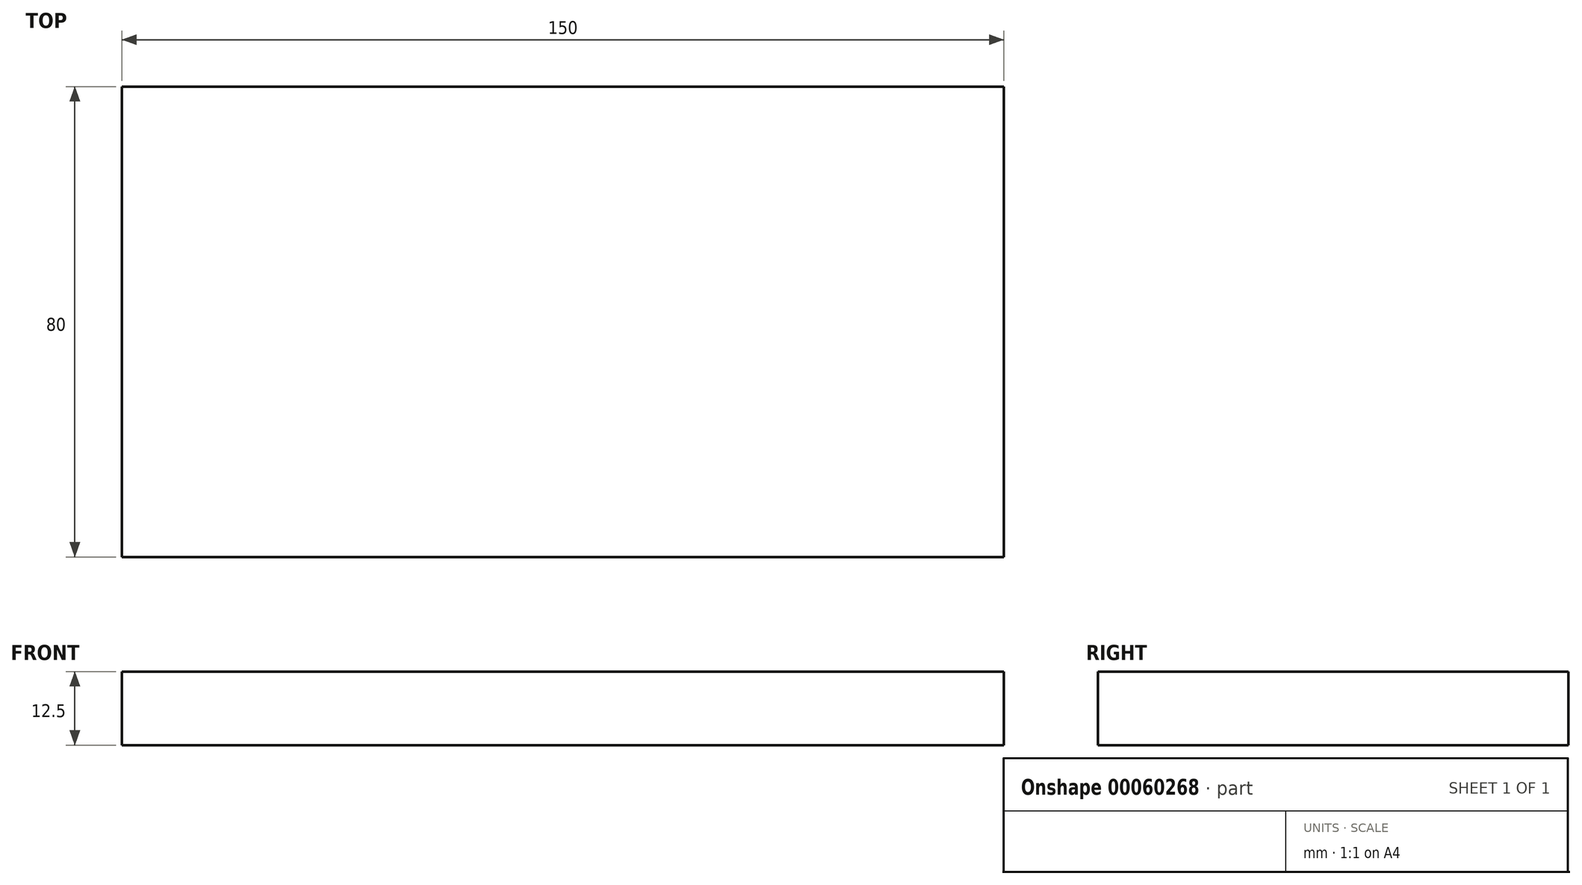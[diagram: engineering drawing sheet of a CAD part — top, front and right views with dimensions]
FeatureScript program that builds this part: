
annotation { "Feature Type Name" : "Feature", "Feature Type Description" : "" }
export const myFeature = defineFeature(function(context is Context, id is Id, definition is map)
    precondition{}
    {
        {
            var Q0;
            Q0=qCreatedBy(makeId("Top.planeOp"),FACE);
            var sketch = newSketch(context, id + "F0", { "sketchPlane" : qUnion([Q0])});
            skLineSegment(sketch, "E0.rect.bottom", {"start": v(-75, 40) * mm, "end": v(75, 40) * mm});
            skLineSegment(sketch, "E0.rect.top", {"start": v(-75, -40) * mm, "end": v(75, -40) * mm});
            skLineSegment(sketch, "E0.rect.left", {"start": v(-75, 40) * mm, "end": v(-75, -40) * mm});
            skLineSegment(sketch, "E0.rect.right", {"start": v(75, 40) * mm, "end": v(75, -40) * mm});
            skPoint(sketch, "E0.rect.middle", {"position": v(0, 0) * mm});
            skSolve(sketch);
        }
        {
            var Q0;
            Q0=makeQuery(id+"F0.imprint","IMPRINT",FACE,{"disambiguationData":[TD([[makeQuery(id+"F0.imprint","IMPRINT",EDGE,{"derivedFrom":sQuery(id+"F0.wireOp",EDGE,"E0.rect.bottom")}),-1.0]])]});
            extrude(context, id + "F1", {"entities" : qUnion([Q0]), "depth" : 12.5 * mm});
        }
    });
